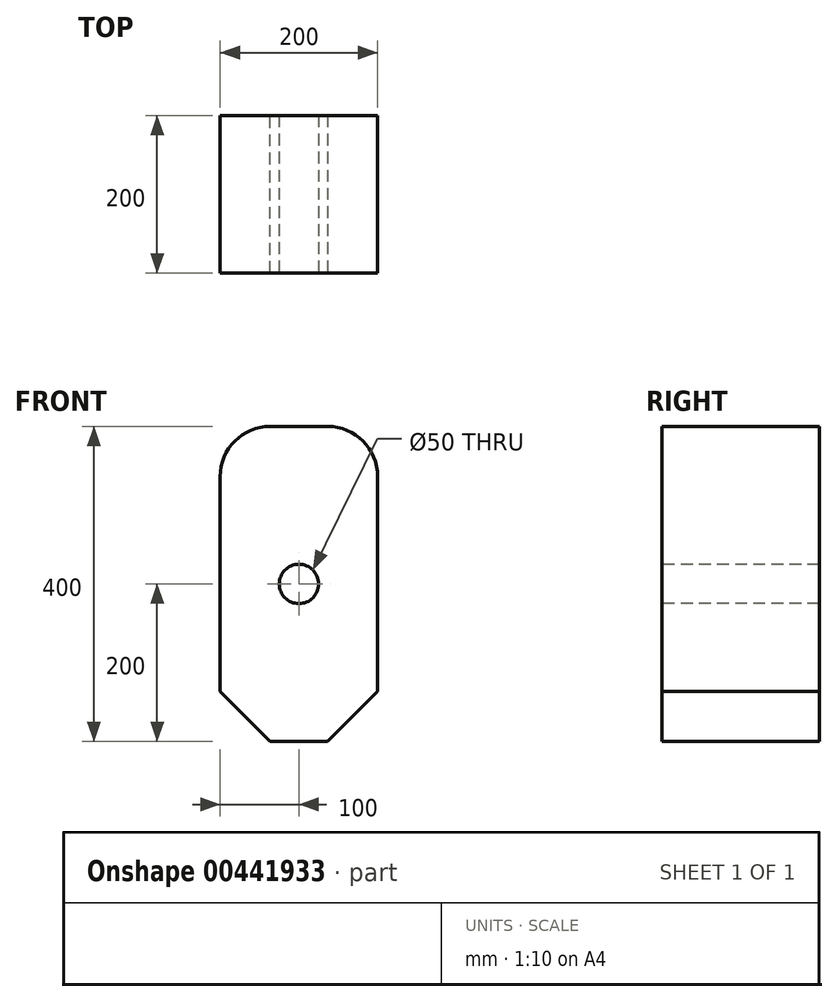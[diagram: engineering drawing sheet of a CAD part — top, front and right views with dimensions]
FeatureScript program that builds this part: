
annotation { "Feature Type Name" : "Feature", "Feature Type Description" : "" }
export const myFeature = defineFeature(function(context is Context, id is Id, definition is map)
    precondition{}
    {
        {
            var Q0;
            Q0=qCreatedBy(makeId("Front.planeOp"),FACE);
            var sketch = newSketch(context, id + "F0", { "sketchPlane" : qUnion([Q0])});
            skLineSegment(sketch, "E0.bottom", {"start": v(100, 200) * mm, "end": v(-100, 200) * mm});
            skLineSegment(sketch, "E0.top", {"start": v(100, -200) * mm, "end": v(-100, -200) * mm});
            skLineSegment(sketch, "E0.left", {"start": v(100, 200) * mm, "end": v(100, -200) * mm});
            skLineSegment(sketch, "E0.right", {"start": v(-100, 200) * mm, "end": v(-100, -200) * mm});
            skPoint(sketch, "E0.middle", {"position": v(0, 0) * mm});
            skSolve(sketch);
        }
        {
            var Q0;
            Q0 = qSketchRegion(id + "F0", true);
            extrude(context, id + "F1", {"entities" : qUnion([Q0]), "depth" : 200 * mm});
        }
        {
            var Q0;
            Q0=makeQuery(id+"F1.opExtrude","CAP_FACE",FACE,{"disambiguationData":[OSD([sQuery(id+"F0.wireOp",EDGE,"E0.bottom"),sQuery(id+"F0.wireOp",EDGE,"E0.top"),sQuery(id+"F0.wireOp",EDGE,"E0.left"),sQuery(id+"F0.wireOp",EDGE,"E0.right")])],"isStart":false});
            var sketch = newSketch(context, id + "F2", { "sketchPlane" : qUnion([Q0])});
            skCircle(sketch, "E1", {"center": v(0, 0) * mm, "radius": 25 * mm});
            skSolve(sketch);
        }
        {
            var Q0;
            Q0=makeQuery(id+"F2.imprint","IMPRINT",FACE,{"disambiguationData":[TD([[makeQuery(id+"F2.imprint","IMPRINT",EDGE,{"derivedFrom":sQuery(id+"F2.wireOp",EDGE,"E1")}),1.0]])]});
            extrude(context, id + "F3", {"entities" : qUnion([Q0]), "operationType" : NewBodyOperationType.REMOVE, "endBound" : BoundingType.THROUGH_ALL, "oppositeDirection" : true, "depth" : 25.4 * mm});
        }
        {
            var Q0;
            Q0=makeQuery(id+"F1.opExtrude","SWEPT_EDGE",EDGE,{"disambiguationData":[OSD([sQuery(id+"F0.wireOp",EDGE,"E0.bottom"),sQuery(id+"F0.wireOp",EDGE,"E0.left")])]});
            var Q1;
            Q1=makeQuery(id+"F1.opExtrude","SWEPT_EDGE",EDGE,{"disambiguationData":[OSD([sQuery(id+"F0.wireOp",EDGE,"E0.bottom"),sQuery(id+"F0.wireOp",EDGE,"E0.right")])]});
            fillet(context, id + "F4", {"entities" : qUnion([Q0, Q1]), "radius" : 63.5 * mm, "tangentPropagation" : true, "allowEdgeOverflow" : false});
        }
        {
            var Q0;
            Q0=makeQuery(id+"F1.opExtrude","SWEPT_EDGE",EDGE,{"disambiguationData":[OSD([sQuery(id+"F0.wireOp",EDGE,"E0.top"),sQuery(id+"F0.wireOp",EDGE,"E0.right")])]});
            var Q1;
            Q1=makeQuery(id+"F1.opExtrude","SWEPT_EDGE",EDGE,{"disambiguationData":[OSD([sQuery(id+"F0.wireOp",EDGE,"E0.top"),sQuery(id+"F0.wireOp",EDGE,"E0.left")])]});
            chamfer(context, id + "F5", {"entities" : qUnion([Q0, Q1]), "width" : 63.5 * mm, "tangentPropagation" : true});
        }
    });
